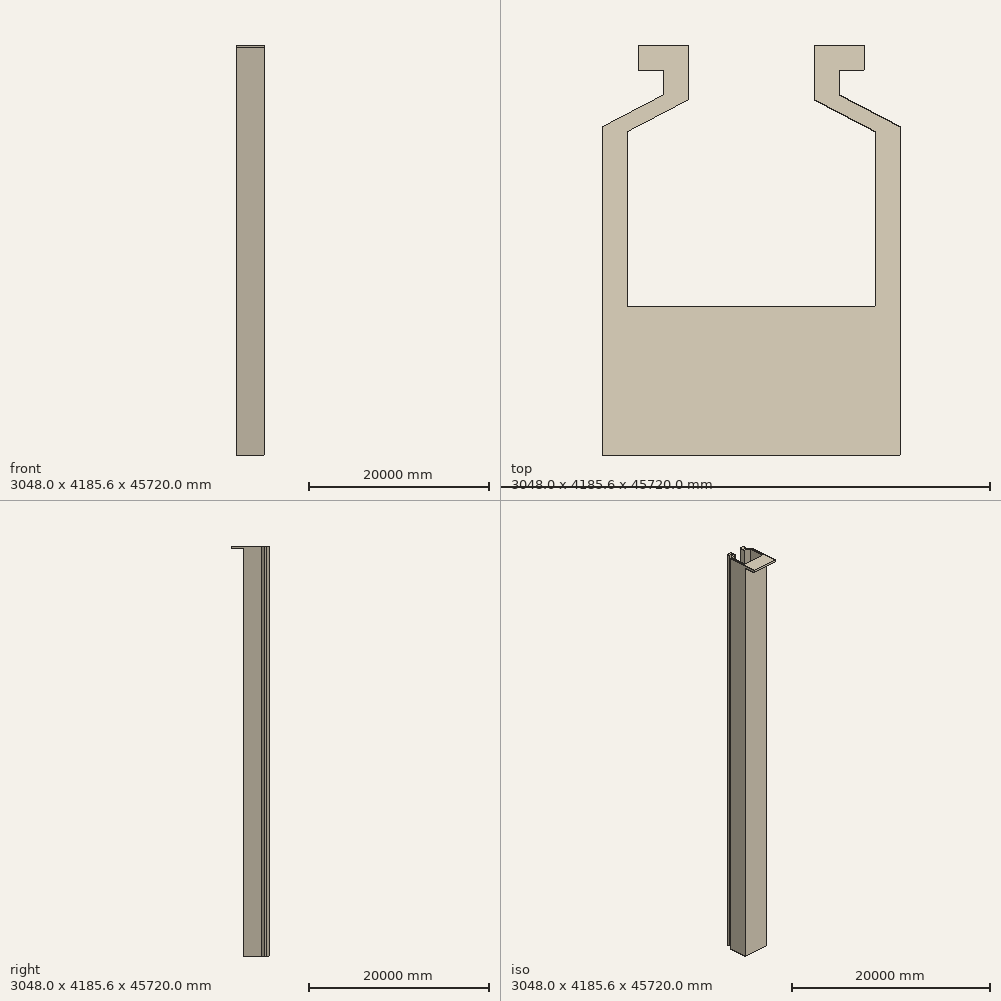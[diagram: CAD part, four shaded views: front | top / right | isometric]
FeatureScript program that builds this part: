
annotation { "Feature Type Name" : "Feature", "Feature Type Description" : "" }
export const myFeature = defineFeature(function(context is Context, id is Id, definition is map)
    precondition{}
    {
        {
            var Q0;
            Q0=qCreatedBy(makeId("Top.planeOp"),FACE);
            var sketch = newSketch(context, id + "F0", { "sketchPlane" : qUnion([Q0])});
            skLineSegment(sketch, "E0", {"start": v(0, 2540) * mm, "end": v(0, 0) * mm, "construction": true});
            skLineSegment(sketch, "E1", {"start": v(0, 0) * mm, "end": v(0, 254) * mm});
            skLineSegment(sketch, "E2", {"start": v(0, 254) * mm, "end": v(1270, 254) * mm});
            skLineSegment(sketch, "E3", {"start": v(0, 0) * mm, "end": v(1524, 0) * mm});
            skLineSegment(sketch, "E4", {"start": v(1524, 0) * mm, "end": v(1524, 2082.8) * mm});
            skLineSegment(sketch, "E5", {"start": v(1524, 2082.8) * mm, "end": v(902.12, 2407.62) * mm});
            skLineSegment(sketch, "E6", {"start": v(902.12, 2407.62) * mm, "end": v(902.12, 2661.62) * mm});
            skLineSegment(sketch, "E7", {"start": v(902.12, 2661.62) * mm, "end": v(1156.12, 2661.62) * mm});
            skLineSegment(sketch, "E8", {"start": v(1156.12, 2661.62) * mm, "end": v(1156.12, 2915.62) * mm});
            skLineSegment(sketch, "E9", {"start": v(1270, 254) * mm, "end": v(1270, 2032) * mm});
            skLineSegment(sketch, "E10", {"start": v(1270, 2032) * mm, "end": v(648.12, 2356.82) * mm});
            skLineSegment(sketch, "E11", {"start": v(648.12, 2356.82) * mm, "end": v(648.12, 2915.62) * mm});
            skPoint(sketch, "E12.end.orphan", {"position": v(674.93, 2915.62) * mm});
            skLineSegment(sketch, "E13", {"start": v(648.12, 2915.62) * mm, "end": v(1156.12, 2915.62) * mm});
            skLineSegment(sketch, "E14", {"start": v(0, 254) * mm, "end": v(0, 0) * mm});
            skSolve(sketch);
        }
        {
            var Q0;
            Q0 = qSketchRegion(id + "F0", true);
            extrude(context, id + "F1", {"entities" : qUnion([Q0]), "oppositeDirection" : true, "depth" : 45720 * mm});
        }
        {
            var Q0;
            Q0=makeQuery(id+"F1.opExtrude","SWEPT_BODY",BODY,{"disambiguationData":[OSD([sQuery(id+"F0.wireOp",EDGE,"E2"),sQuery(id+"F0.wireOp",EDGE,"E3"),sQuery(id+"F0.wireOp",EDGE,"E4"),sQuery(id+"F0.wireOp",EDGE,"E5"),sQuery(id+"F0.wireOp",EDGE,"E6"),sQuery(id+"F0.wireOp",EDGE,"E7"),sQuery(id+"F0.wireOp",EDGE,"E8"),sQuery(id+"F0.wireOp",EDGE,"E9"),sQuery(id+"F0.wireOp",EDGE,"E10"),sQuery(id+"F0.wireOp",EDGE,"E11"),sQuery(id+"F0.wireOp",EDGE,"E13"),sQuery(id+"F0.wireOp",EDGE,"E14")])]});
            var Q1;
            Q1=qCreatedBy(makeId("Right.planeOp"),FACE);
            mirror(context, id + "F2", {"operationType" : NewBodyOperationType.ADD, "entities" : qUnion([Q0]), "mirrorPlane" : qUnion([Q1])});
        }
        {
            var Q0;
            {var subQ0=makeQuery(id+"F1.opExtrude","SWEPT_FACE",FACE,{"disambiguationData":[OSD([sQuery(id+"F0.wireOp",EDGE,"E3")])]});Q0=makeQuery(id+"F2.boolean.opBoolean","MERGE",FACE,{"derivedFrom":[subQ0,makeQuery(id+"F2.opPattern","COPY",FACE,{"derivedFrom":subQ0,"instanceName":"1"})]});}
            var sketch = newSketch(context, id + "F3", { "sketchPlane" : qUnion([Q0])});
            skLineSegment(sketch, "E15", {"start": v(1524, 0) * mm, "end": v(-1524, 0) * mm});
            skLineSegment(sketch, "E16", {"start": v(-1524, 0) * mm, "end": v(-1524, -254) * mm});
            skLineSegment(sketch, "E17", {"start": v(-1524, -254) * mm, "end": v(1524, -254) * mm});
            skLineSegment(sketch, "E18", {"start": v(1524, -254) * mm, "end": v(1524, 0) * mm});
            skSolve(sketch);
        }
        {
            var Q0;
            Q0 = qSketchRegion(id + "F3", true);
            extrude(context, id + "F4", {"entities" : qUnion([Q0]), "operationType" : NewBodyOperationType.ADD, "depth" : 1270 * mm});
        }
    });
